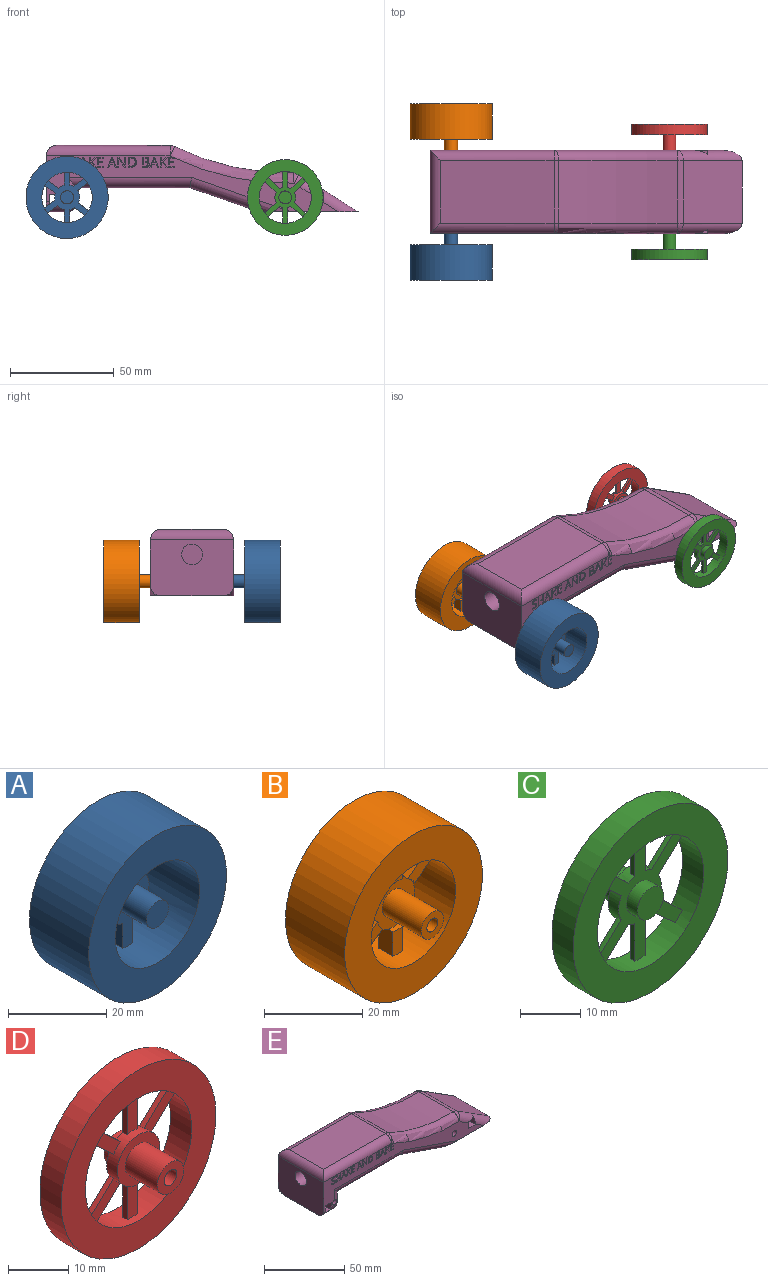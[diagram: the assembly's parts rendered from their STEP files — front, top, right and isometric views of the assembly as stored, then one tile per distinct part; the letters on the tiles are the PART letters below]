
ASSEMBLY  parts=5 mates=4
PART A: 42 faces, bbox 39.6x22.4x39.6 mm
  f0: cylinder r=12.1mm len=24.2mm, axis (0,1,0), area 1225mm2, adj f2,f3,f4,f5,f6,f7,f8,f9
  f1: cylinder r=19.8mm len=39.6mm, axis (0,1,0), area 2114.9mm2, adj f2,f3
  f2: plane 39.6x39.6mm, normal (0,-1,0), area 771.7mm2, adj f0,f1
  f3: plane 39.6x39.6mm, normal (0,1,0), area 771.7mm2, adj f0,f1
  f4: plane 6.21x2.8mm, normal (0,1,0), area 17mm2, adj f0,f15,f16,f17
  f5: plane 24.22x21.29mm, normal (0,-1,0), area 186.2mm2, adj f0,f15,f16,f18,f19,f20,f22,f23
  f6: plane 6.21x2.8mm, normal (0,1,0), area 17mm2, adj f0,f19,f20,f21
  f7: plane 7.08x5.81mm, normal (0,1,0), area 17.6mm2, adj f0,f23,f24,f25
  f8: plane 6.48x6.25mm, normal (0,1,0), area 17.6mm2, adj f0,f28,f29,f30
  f9: plane 6.48x5.97mm, normal (0,1,0), area 17mm2, adj f0,f32,f33,f34
  f10: plane 6.85x5.92mm, normal (0,1,0), area 17.5mm2, adj f0,f37,f38,f39
  f11: cylinder r=3.17mm len=11.2mm, axis (0,1,0), area 223.1mm2, adj f13,f26
  f12: cylinder r=1.57mm len=13.9mm, axis (0,1,0), area 137.1mm2, adj f13,f14
  f13: plane 6.34x6.34mm, normal (0,1,0), area 23.8mm2, adj f11,f12
  f14: plane 3.14x3.14mm, normal (0,1,0), area 7.7mm2, adj f12
  f15: plane 6.11x4mm, normal (1,0,0), area 24.4mm2, adj f0,f4,f5,f17,f27
  f16: plane 6.12x4mm, normal (-1,0,0), area 24.5mm2, adj f0,f4,f5,f17,f18
  f17: cylinder r=6.07mm len=2.8mm, axis (0,-1,0), area 3.7mm2, adj f4,f15,f16,f26
  f18: cylinder r=6.07mm len=2.75mm, axis (0,-1,0), area 8.6mm2, adj f5,f16,f26,f34
  f19: plane 6.12x4mm, normal (-1,0,0), area 24.5mm2, adj f0,f5,f6,f21,f35
  f20: plane 6.11x4mm, normal (1,0,0), area 24.4mm2, adj f0,f5,f6,f21,f22
  f21: cylinder r=6.07mm len=2.8mm, axis (0,-1,0), area 3.7mm2, adj f6,f19,f20,f26
  f22: cylinder r=6.07mm len=2.7mm, axis (0,-1,0), area 6.8mm2, adj f5,f20,f26,f38
  f23: plane 5.22x4mm, normal (-0.59,0,0.8), area 25.4mm2, adj f0,f5,f7,f24,f26,f27
  f24: cylinder r=5.88mm len=2.07mm, axis (0,-1,0), area 3.7mm2, adj f7,f23,f25,f26
  f25: plane 5x4mm, normal (0.59,0,-0.8), area 24.4mm2, adj f0,f5,f7,f24,f26,f36
  f26: plane 12.14x12.14mm, normal (0,1,0), area 82.6mm2, adj f11,f17,f18,f21,f22,f23,f24,f25
  f27: cylinder r=6.07mm len=2.7mm, axis (0,-1,0), area 4.9mm2, adj f5,f15,f23,f26
  f28: cylinder r=5.88mm len=2.55mm, axis (0,-1,0), area 3.7mm2, adj f8,f26,f29,f30
  f29: plane 5.22x4mm, normal (-0.59,0,0.8), area 25.4mm2, adj f0,f5,f8,f26,f28,f31
  f30: plane 5x4mm, normal (0.59,0,-0.8), area 24.4mm2, adj f0,f5,f8,f26,f28,f35
  f31: cylinder r=6.07mm len=3.38mm, axis (0,-1,0), area 9.3mm2, adj f5,f26,f29,f32
  f32: plane 4.96x4mm, normal (-0.59,0,-0.8), area 24.7mm2, adj f0,f5,f9,f31,f33
  f33: cylinder r=6.07mm len=2.36mm, axis (0,-1,0), area 3.7mm2, adj f9,f26,f32,f34
  f34: plane 4.88x4mm, normal (0.59,0,0.8), area 24.3mm2, adj f0,f5,f9,f18,f33
  f35: cylinder r=6.07mm len=3.19mm, axis (0,-1,0), area 10.3mm2, adj f5,f19,f26,f30
  f36: cylinder r=6.07mm len=6.03mm, axis (0,-1,0), area 17.1mm2, adj f5,f25,f26,f39
  f37: cylinder r=5.88mm len=2.14mm, axis (0,-1,0), area 3.7mm2, adj f10,f26,f38,f39
  f38: plane 5.12x4mm, normal (-0.59,0,-0.8), area 24.9mm2, adj f0,f5,f10,f22,f26,f37
  f39: plane 5.04x4mm, normal (0.59,0,0.8), area 24.5mm2, adj f0,f5,f10,f26,f36,f37
  f40: plane 6.32x6.32mm, normal (0,-1,0), area 31.4mm2, adj f41
  f41: cylinder r=3.16mm len=8.5mm, axis (0,1,0), area 168.9mm2, adj f5,f40
PART B: 42 faces, bbox 39.6x22.4x39.6 mm
  f0: cylinder r=12.1mm len=24.2mm, axis (0,-1,0), area 1225mm2, adj f2,f3,f4,f5,f6,f7,f8,f9
  f1: cylinder r=19.8mm len=39.6mm, axis (0,-1,0), area 2114.9mm2, adj f2,f3
  f2: plane 39.6x39.6mm, normal (0,1,0), area 771.7mm2, adj f0,f1
  f3: plane 39.6x39.6mm, normal (0,-1,0), area 771.7mm2, adj f0,f1
  f4: plane 6.21x2.8mm, normal (0,-1,0), area 17mm2, adj f0,f15,f16,f17
  f5: plane 24.22x21.29mm, normal (0,1,0), area 186.3mm2, adj f0,f15,f16,f18,f19,f20,f22,f23
  f6: plane 6.21x2.8mm, normal (0,-1,0), area 17mm2, adj f0,f19,f20,f21
  f7: plane 7.08x5.81mm, normal (0,-1,0), area 17.6mm2, adj f0,f23,f24,f25
  f8: plane 6.48x6.25mm, normal (0,-1,0), area 17.6mm2, adj f0,f28,f29,f30
  f9: plane 6.48x5.97mm, normal (0,-1,0), area 17mm2, adj f0,f32,f33,f34
  f10: plane 6.85x5.92mm, normal (0,-1,0), area 17.5mm2, adj f0,f37,f38,f39
  f11: cylinder r=3.17mm len=11.2mm, axis (0,-1,0), area 223.1mm2, adj f13,f26
  f12: cylinder r=1.57mm len=13.9mm, axis (0,-1,0), area 137.1mm2, adj f13,f14
  f13: plane 6.34x6.34mm, normal (0,-1,0), area 23.8mm2, adj f11,f12
  f14: plane 3.14x3.14mm, normal (0,-1,0), area 7.7mm2, adj f12
  f15: plane 6.11x4mm, normal (1,0,0), area 24.4mm2, adj f0,f4,f5,f17,f27
  f16: plane 6.12x4mm, normal (-1,0,0), area 24.5mm2, adj f0,f4,f5,f17,f18
  f17: cylinder r=6.07mm len=2.8mm, axis (0,1,0), area 3.7mm2, adj f4,f15,f16,f26
  f18: cylinder r=6.07mm len=2.75mm, axis (0,1,0), area 8.6mm2, adj f5,f16,f26,f34
  f19: plane 6.12x4mm, normal (-1,0,0), area 24.5mm2, adj f0,f5,f6,f21,f35
  f20: plane 6.11x4mm, normal (1,0,0), area 24.4mm2, adj f0,f5,f6,f21,f22
  f21: cylinder r=6.07mm len=2.8mm, axis (0,1,0), area 3.7mm2, adj f6,f19,f20,f26
  f22: cylinder r=6.07mm len=2.7mm, axis (0,1,0), area 6.8mm2, adj f5,f20,f26,f38
  f23: plane 5.22x4mm, normal (-0.59,0,0.8), area 25.4mm2, adj f0,f5,f7,f24,f26,f27
  f24: cylinder r=5.88mm len=2.07mm, axis (0,1,0), area 3.7mm2, adj f7,f23,f25,f26
  f25: plane 5x4mm, normal (0.59,0,-0.8), area 24.4mm2, adj f0,f5,f7,f24,f26,f36
  f26: plane 12.14x12.14mm, normal (0,-1,0), area 82.6mm2, adj f11,f17,f18,f21,f22,f23,f24,f25
  f27: cylinder r=6.07mm len=2.7mm, axis (0,1,0), area 4.9mm2, adj f5,f15,f23,f26
  f28: cylinder r=5.88mm len=2.55mm, axis (0,1,0), area 3.7mm2, adj f8,f26,f29,f30
  f29: plane 5.22x4mm, normal (-0.59,0,0.8), area 25.4mm2, adj f0,f5,f8,f26,f28,f31
  f30: plane 5x4mm, normal (0.59,0,-0.8), area 24.4mm2, adj f0,f5,f8,f26,f28,f35
  f31: cylinder r=6.07mm len=3.38mm, axis (0,1,0), area 9.3mm2, adj f5,f26,f29,f32
  f32: plane 4.96x4mm, normal (-0.59,0,-0.8), area 24.7mm2, adj f0,f5,f9,f31,f33
  f33: cylinder r=6.07mm len=2.36mm, axis (0,1,0), area 3.7mm2, adj f9,f26,f32,f34
  f34: plane 4.88x4mm, normal (0.59,0,0.8), area 24.3mm2, adj f0,f5,f9,f18,f33
  f35: cylinder r=6.07mm len=3.19mm, axis (0,1,0), area 10.3mm2, adj f5,f19,f26,f30
  f36: cylinder r=6.07mm len=6.03mm, axis (0,1,0), area 17.1mm2, adj f5,f25,f26,f39
  f37: cylinder r=5.88mm len=2.14mm, axis (0,1,0), area 3.7mm2, adj f10,f26,f38,f39
  f38: plane 5.12x4mm, normal (-0.59,0,-0.8), area 24.9mm2, adj f0,f5,f10,f22,f26,f37
  f39: plane 5.04x4mm, normal (0.59,0,0.8), area 24.5mm2, adj f0,f5,f10,f26,f36,f37
  f40: plane 6.32x6.32mm, normal (0,1,0), area 31.4mm2, adj f41
  f41: cylinder r=3.16mm len=8.5mm, axis (0,-1,0), area 168.9mm2, adj f5,f40
PART C: 31 faces, bbox 36.4x12.5x36.4 mm
  f0: cylinder r=3.1mm len=7.5mm, axis (0,1,0), area 146.1mm2, adj f2,f5
  f1: cylinder r=1.5mm len=10mm, axis (0,1,0), area 94.2mm2, adj f2,f3
  f2: plane 6.2x6.2mm, normal (0,1,0), area 23.1mm2, adj f0,f1
  f3: plane 3x3mm, normal (0,1,0), area 7.1mm2, adj f1
  f4: cylinder r=5mm len=10mm, axis (0,-1,0), area 64mm2, adj f5,f6,f9,f10,f11,f12,f13,f14
  f5: plane 10x10mm, normal (0,1,0), area 48.3mm2, adj f0,f4
  f6: plane 25.02x19.87mm, normal (0,-1,0), area 156.8mm2, adj f4,f8,f9,f10,f12,f13,f15,f16
  f7: plane 6.18x6.18mm, normal (0,-1,0), area 30mm2, adj f8
  f8: cylinder r=3.09mm len=6.18mm, axis (0,1,0), area 48.5mm2, adj f6,f7
  f9: plane 5.55x5.17mm, normal (0.68,0,-0.73), area 7.6mm2, adj f4,f6,f11,f27
  f10: plane 5.55x5.17mm, normal (-0.68,0,0.73), area 7.6mm2, adj f4,f6,f11,f27
  f11: plane 7.19x6.93mm, normal (0,1,0), area 18.1mm2, adj f4,f9,f10,f27
  f12: plane 7.59x1mm, normal (1,0,0), area 7.6mm2, adj f4,f6,f14,f27
  f13: plane 7.59x1mm, normal (-1,0,0), area 7.6mm2, adj f4,f6,f14,f27
  f14: plane 7.65x2.4mm, normal (0,1,0), area 18.1mm2, adj f4,f12,f13,f27
  f15: plane 5.55x5.17mm, normal (-0.68,0,-0.73), area 7.6mm2, adj f4,f6,f17,f27
  f16: plane 5.55x5.17mm, normal (0.68,0,0.73), area 7.6mm2, adj f4,f6,f17,f27
  f17: plane 7.19x6.93mm, normal (0,1,0), area 18.1mm2, adj f4,f15,f16,f27
  f18: plane 5.55x5.17mm, normal (-0.68,0,0.73), area 7.6mm2, adj f4,f6,f20,f27
  f19: plane 5.55x5.17mm, normal (0.68,0,-0.73), area 7.6mm2, adj f4,f6,f20,f27
  f20: plane 7.19x6.93mm, normal (0,1,0), area 18.1mm2, adj f4,f18,f19,f27
  f21: plane 7.59x1mm, normal (-1,0,0), area 7.6mm2, adj f4,f6,f23,f27
  f22: plane 7.59x1mm, normal (1,0,0), area 7.6mm2, adj f4,f6,f23,f27
  f23: plane 7.65x2.4mm, normal (0,1,0), area 18.1mm2, adj f4,f21,f22,f27
  f24: plane 5.55x5.17mm, normal (-0.68,0,-0.73), area 7.6mm2, adj f4,f6,f26,f27
  f25: plane 5.55x5.17mm, normal (0.68,0,0.73), area 7.6mm2, adj f4,f6,f26,f27
  f26: plane 7.19x6.93mm, normal (0,1,0), area 18.1mm2, adj f4,f24,f25,f27
  f27: cylinder r=12.5mm len=25mm, axis (0,1,0), area 378.3mm2, adj f6,f9,f10,f11,f12,f13,f14,f15
  f28: cylinder r=18.2mm len=36.4mm, axis (0,1,0), area 571.8mm2, adj f29,f30
  f29: plane 36.4x36.4mm, normal (0,-1,0), area 549.7mm2, adj f27,f28
  f30: plane 36.4x36.4mm, normal (0,1,0), area 549.7mm2, adj f27,f28
PART D: 31 faces, bbox 36.4x12.5x36.4 mm
  f0: cylinder r=3.1mm len=7.5mm, axis (0,-1,0), area 146.1mm2, adj f2,f5
  f1: cylinder r=1.5mm len=10mm, axis (0,-1,0), area 94.2mm2, adj f2,f3
  f2: plane 6.2x6.2mm, normal (0,-1,0), area 23.1mm2, adj f0,f1
  f3: plane 3x3mm, normal (0,-1,0), area 7.1mm2, adj f1
  f4: cylinder r=5mm len=10mm, axis (0,1,0), area 64mm2, adj f5,f6,f9,f10,f11,f12,f13,f14
  f5: plane 10x10mm, normal (0,-1,0), area 48.3mm2, adj f0,f4
  f6: plane 25.02x19.87mm, normal (0,1,0), area 156.8mm2, adj f4,f8,f9,f10,f12,f13,f15,f16
  f7: plane 6.18x6.18mm, normal (0,1,0), area 30mm2, adj f8
  f8: cylinder r=3.09mm len=6.18mm, axis (0,-1,0), area 48.5mm2, adj f6,f7
  f9: plane 5.55x5.17mm, normal (0.68,0,-0.73), area 7.6mm2, adj f4,f6,f11,f27
  f10: plane 5.55x5.17mm, normal (-0.68,0,0.73), area 7.6mm2, adj f4,f6,f11,f27
  f11: plane 7.19x6.93mm, normal (0,-1,0), area 18.1mm2, adj f4,f9,f10,f27
  f12: plane 7.59x1mm, normal (1,0,0), area 7.6mm2, adj f4,f6,f14,f27
  f13: plane 7.59x1mm, normal (-1,0,0), area 7.6mm2, adj f4,f6,f14,f27
  f14: plane 7.65x2.4mm, normal (0,-1,0), area 18.1mm2, adj f4,f12,f13,f27
  f15: plane 5.55x5.17mm, normal (-0.68,0,-0.73), area 7.6mm2, adj f4,f6,f17,f27
  f16: plane 5.55x5.17mm, normal (0.68,0,0.73), area 7.6mm2, adj f4,f6,f17,f27
  f17: plane 7.19x6.93mm, normal (0,-1,0), area 18.1mm2, adj f4,f15,f16,f27
  f18: plane 5.55x5.17mm, normal (-0.68,0,0.73), area 7.6mm2, adj f4,f6,f20,f27
  f19: plane 5.55x5.17mm, normal (0.68,0,-0.73), area 7.6mm2, adj f4,f6,f20,f27
  f20: plane 7.19x6.93mm, normal (0,-1,0), area 18.1mm2, adj f4,f18,f19,f27
  f21: plane 7.59x1mm, normal (-1,0,0), area 7.6mm2, adj f4,f6,f23,f27
  f22: plane 7.59x1mm, normal (1,0,0), area 7.6mm2, adj f4,f6,f23,f27
  f23: plane 7.65x2.4mm, normal (0,-1,0), area 18.1mm2, adj f4,f21,f22,f27
  f24: plane 5.55x5.17mm, normal (-0.68,0,-0.73), area 7.6mm2, adj f4,f6,f26,f27
  f25: plane 5.55x5.17mm, normal (0.68,0,0.73), area 7.6mm2, adj f4,f6,f26,f27
  f26: plane 7.19x6.93mm, normal (0,-1,0), area 18.1mm2, adj f4,f24,f25,f27
  f27: cylinder r=12.5mm len=25mm, axis (0,-1,0), area 378.3mm2, adj f6,f9,f10,f11,f12,f13,f14,f15
  f28: cylinder r=18.2mm len=36.4mm, axis (0,-1,0), area 571.8mm2, adj f29,f30
  f29: plane 36.4x36.4mm, normal (0,1,0), area 549.7mm2, adj f27,f28
  f30: plane 36.4x36.4mm, normal (0,-1,0), area 549.7mm2, adj f27,f28
PART E: 246 faces, bbox 150x40x36.7 mm
  f0: cylinder r=5mm len=0.13mm, axis (0,0,1), area 0mm2, adj f2,f9,f244
  f1: cylinder r=5mm len=11.7mm, axis (0,0,-1), area 59.9mm2, adj f3,f9,f30,f237,f239
  f2: plane 140.79x27mm, normal (0,-1,0), area 1223.2mm2, adj f0,f4,f5,f9,f10,f15,f21,f26
  f3: plane 140.79x27mm, normal (0,1,0), area 1319.6mm2, adj f1,f4,f5,f9,f10,f16,f19,f24
  f4: plane 46.54x40mm, normal (0,0,-1), area 1815mm2, adj f2,f3,f14,f15,f16,f28,f236,f241
  f5: plane 40x27mm, normal (-1,0,0), area 990.7mm2, adj f2,f3,f6,f7,f23,f240,f245
  f6: plane 30x9.87mm, normal (0,0,-1), area 296.1mm2, adj f5,f235,f240,f245
  f7: cylinder r=5mm len=60mm, axis (-1,0,0), area 1885mm2, adj f5,f8
  f8: plane 10x10mm, normal (-1,0,0), area 78.5mm2, adj f7
  f9: cylinder r=2mm len=40mm, axis (0,-1,0), area 499.6mm2, adj f0,f1,f2,f3,f238,f243
  f10: cylinder r=2mm len=40mm, axis (0,-1,0), area 502.7mm2, adj f2,f3
  f11: plane 54.55x30mm, normal (0,0,1), area 1636.4mm2, adj f20,f21,f23,f24
  f12: cylinder r=121.86mm len=57.18mm, axis (0,-1,0), area 1773.9mm2, adj f17,f19,f20,f26
  f13: plane 30x28.24mm, normal (0.54,0,0.84), area 1005.1mm2, adj f14,f15,f16,f17
  f14: cylinder r=5mm len=34.16mm, axis (0,1,0), area 24.9mm2, adj f4,f13,f15,f16
  f15: cylinder r=5mm len=30.93mm, axis (-0.84,0,0.54), area 223mm2, adj f2,f4,f13,f14,f25,f32,f33,f34
  f16: cylinder r=5mm len=30.93mm, axis (0.84,0,-0.54), area 223mm2, adj f3,f4,f13,f14,f18,f32,f33,f34
  f17: cylinder r=5mm len=30mm, axis (0,-1,0), area 89mm2, adj f12,f13,f18,f25
  f18: sphere r=5mm, area 14.8mm2, adj f16,f17,f19
  f19: torus R=126.86mm, axis (0,-1,0), area 471.3mm2, adj f3,f12,f18,f22
  f20: cylinder r=5mm len=30mm, axis (0,-1,0), area 69mm2, adj f11,f12,f22,f27
  f21: cylinder r=5mm len=59.55mm, axis (-1,0,0), area 453.4mm2, adj f2,f11,f23,f27
  f22: sphere r=5mm, area 11.5mm2, adj f19,f20,f24
  f23: cylinder r=5mm len=40mm, axis (0,-1,0), area 285.6mm2, adj f5,f11,f21,f24
  f24: cylinder r=5mm len=59.55mm, axis (1,0,0), area 453.4mm2, adj f3,f11,f22,f23
  f25: sphere r=5mm, area 14.8mm2, adj f15,f17,f26
  f26: torus R=126.86mm, axis (0,-1,0), area 471.2mm2, adj f2,f12,f25,f27,f47,f48
  f27: sphere r=5mm, area 11.5mm2, adj f20,f21,f26
  f28: plane 33.64x30mm, normal (-0.33,0,-0.94), area 1068.5mm2, adj f4,f29,f236,f241
  f29: plane 54.2x30mm, normal (0,0,-1), area 1625.9mm2, adj f28,f30,f237,f242
  f30: plane 30x6.7mm, normal (1,0,0), area 201mm2, adj f1,f29,f235,f243
  f31: plane 40x6.08mm, normal (0,0,1), area 243.2mm2, adj f2,f3,f32,f33
  f32: plane 40x5.07mm, normal (1,0,0), area 202.6mm2, adj f2,f3,f15,f16,f31,f34
  f33: plane 40x5.07mm, normal (-1,0,0), area 196.8mm2, adj f2,f3,f15,f16,f31,f34
  f34: plane 39.89x6.08mm, normal (0,0,-1), area 234.1mm2, adj f15,f16,f32,f33
  f35: plane 40x5.58mm, normal (1,0,0), area 222.6mm2, adj f2,f3,f36,f38,f240,f245
  f36: plane 39.17x5.11mm, normal (0,0,1), area 200mm2, adj f35,f37,f240,f245
  f37: plane 40x5.58mm, normal (-1,0,0), area 222.6mm2, adj f2,f3,f36,f38,f240,f245
  f38: plane 40x5.11mm, normal (0,0,-1), area 204.3mm2, adj f2,f3,f35,f37
  f39: plane 1x0.5mm, normal (-1,0,0), area 0.5mm2, adj f2,f40,f50,f51
  f40: plane 2.12x1mm, normal (0,0,-1), area 2.1mm2, adj f2,f39,f41,f51
  f41: plane 1.77x1mm, normal (-1,0,0), area 1.8mm2, adj f2,f40,f42,f51
  f42: plane 1.99x1mm, normal (0,0,1), area 2mm2, adj f2,f41,f43,f51
  f43: plane 1x0.49mm, normal (-1,0,0), area 0.5mm2, adj f2,f42,f44,f51
  f44: plane 1.99x1mm, normal (0,0,-1), area 2mm2, adj f2,f43,f45,f51
  f45: plane 1.55x1mm, normal (-1,0,0), area 1.5mm2, adj f2,f44,f46,f51
  f46: plane 2.12x1mm, normal (0,0,1), area 2.1mm2, adj f2,f45,f47,f51
  f47: plane 1x0.5mm, normal (-1,0,0), area 0.5mm2, adj f2,f26,f46,f48,f51
  f48: plane 2.68x1mm, normal (0,0,-1), area 2.7mm2, adj f2,f26,f47,f49,f51
  f49: plane 4.8x1mm, normal (1,0,0), area 4.8mm2, adj f2,f48,f50,f51
  f50: plane 2.68x1mm, normal (0,0,1), area 2.7mm2, adj f2,f39,f49,f51
  f51: plane 4.8x2.68mm, normal (0,-1,0), area 5.8mm2, adj f39,f40,f41,f42,f43,f44,f45,f46
  f52: plane 1x0.58mm, normal (0,0,1), area 0.6mm2, adj f2,f53,f64,f65
  f53: plane 4.82x1.89mm, normal (-0.93,0,-0.36), area 5.2mm2, adj f2,f52,f54,f65
  f54: plane 1x0.47mm, normal (0,0,-1), area 0.5mm2, adj f2,f53,f55,f65
  f55: plane 4.82x1.9mm, normal (0.93,0,-0.37), area 5.2mm2, adj f2,f54,f56,f65
  f56: plane 1x0.57mm, normal (0,0,1), area 0.6mm2, adj f2,f55,f57,f65
  f57: plane 1.53x1mm, normal (-0.93,0,0.36), area 1.6mm2, adj f2,f56,f58,f65
  f58: plane 1.92x1mm, normal (0,0,1), area 1.9mm2, adj f2,f57,f64,f65
  f59: plane 1.55x1mm, normal (0,0,-1), area 1.6mm2, adj f60,f63,f65,f66
  f60: plane 1.49x1mm, normal (-0.94,0,0.35), area 1.6mm2, adj f59,f61,f65,f66
  f61: extruded ~1x0.69mm, area 0.7mm2, adj f60,f62,f65,f66
  f62: extruded ~1x0.69mm, area 0.7mm2, adj f61,f63,f65,f66
  f63: plane 1.49x1mm, normal (0.94,0,0.35), area 1.6mm2, adj f59,f62,f65,f66
  f64: plane 1.53x1mm, normal (0.93,0,0.36), area 1.6mm2, adj f2,f52,f58,f65
  f65: plane 4.82x4.25mm, normal (0,-1,0), area 5.9mm2, adj f52,f53,f54,f55,f56,f57,f58,f59
  f66: plane 2.18x1.55mm, normal (0,-1,0), area 1.6mm2, adj f59,f60,f61,f62,f63
  f67: plane 1x0.58mm, normal (0,0,1), area 0.6mm2, adj f2,f68,f79,f80
  f68: plane 4.82x1.89mm, normal (-0.93,0,-0.36), area 5.2mm2, adj f2,f67,f69,f80
  f69: plane 1x0.47mm, normal (0,0,-1), area 0.5mm2, adj f2,f68,f70,f80
  f70: plane 4.82x1.9mm, normal (0.93,0,-0.37), area 5.2mm2, adj f2,f69,f71,f80
  f71: plane 1x0.57mm, normal (0,0,1), area 0.6mm2, adj f2,f70,f72,f80
  f72: plane 1.53x1mm, normal (-0.93,0,0.36), area 1.6mm2, adj f2,f71,f73,f80
  f73: plane 1.92x1mm, normal (0,0,1), area 1.9mm2, adj f2,f72,f79,f80
  f74: plane 1.55x1mm, normal (0,0,-1), area 1.6mm2, adj f75,f78,f80,f81
  f75: plane 1.49x1mm, normal (-0.94,0,0.35), area 1.6mm2, adj f74,f76,f80,f81
  f76: extruded ~1x0.69mm, area 0.7mm2, adj f75,f77,f80,f81
  f77: extruded ~1x0.69mm, area 0.7mm2, adj f76,f78,f80,f81
  f78: plane 1.49x1mm, normal (0.94,0,0.35), area 1.6mm2, adj f74,f77,f80,f81
  f79: plane 1.53x1mm, normal (0.93,0,0.36), area 1.6mm2, adj f2,f67,f73,f80
  f80: plane 4.82x4.25mm, normal (0,-1,0), area 5.9mm2, adj f67,f68,f69,f70,f71,f72,f73,f74
  f81: plane 2.18x1.55mm, normal (0,-1,0), area 1.6mm2, adj f74,f75,f76,f77,f78
  f82: plane 2.71x2mm, normal (-0.8,0,-0.59), area 3.4mm2, adj f2,f83,f93,f94
  f83: plane 2.09x1.93mm, normal (-0.73,0,0.68), area 2.8mm2, adj f2,f82,f84,f94
  f84: plane 1x0.66mm, normal (0,0,-1), area 0.7mm2, adj f2,f83,f85,f94
  f85: plane 2.38x2.18mm, normal (0.74,0,-0.67), area 3.2mm2, adj f2,f84,f86,f94
  f86: plane 2.38x1mm, normal (-1,0,0), area 2.4mm2, adj f2,f85,f87,f94
  f87: plane 1x0.56mm, normal (0,0,-1), area 0.6mm2, adj f2,f86,f88,f94
  f88: plane 4.8x1mm, normal (1,0,0), area 4.8mm2, adj f2,f87,f89,f94
  f89: plane 1x0.56mm, normal (0,0,1), area 0.6mm2, adj f2,f88,f90,f94
  f90: plane 1.88x1mm, normal (-1,0,0), area 1.9mm2, adj f2,f89,f91,f94
  f91: plane 1x0.5mm, normal (-0.66,0,0.75), area 0.7mm2, adj f2,f90,f92,f94
  f92: plane 2.33x1.75mm, normal (0.8,0,0.6), area 2.9mm2, adj f2,f91,f93,f94
  f93: plane 1x0.66mm, normal (0,0,1), area 0.7mm2, adj f2,f82,f92,f94
  f94: plane 4.8x3.47mm, normal (0,-1,0), area 6.1mm2, adj f82,f83,f84,f85,f86,f87,f88,f89
  f95: plane 4.8x1mm, normal (-1,0,0), area 4.8mm2, adj f2,f96,f109,f110
  f96: plane 1x0.52mm, normal (0,0,-1), area 0.5mm2, adj f2,f95,f97,f110
  f97: plane 2.75x1mm, normal (1,0,0), area 2.8mm2, adj f2,f96,f98,f110
  f98: extruded ~1x0.69mm, area 0.7mm2, adj f2,f97,f99,f110
  f99: extruded ~1x0.57mm, area 0.6mm2, adj f2,f98,f100,f110
  f100: plane 1x0.03mm, normal (0,0,-1), area 0mm2, adj f2,f99,f101,f110
  f101: plane 4.01x2.62mm, normal (-0.84,0,-0.55), area 4.8mm2, adj f2,f100,f102,f110
  f102: plane 1x0.63mm, normal (0,0,-1), area 0.6mm2, adj f2,f101,f103,f110
  f103: plane 4.8x1mm, normal (1,0,0), area 4.8mm2, adj f2,f102,f104,f110
  f104: plane 1x0.52mm, normal (0,0,1), area 0.5mm2, adj f2,f103,f105,f110
  f105: plane 2.73x1mm, normal (-1,0,0), area 2.7mm2, adj f2,f104,f106,f110
  f106: extruded ~1.3x1mm, area 1.3mm2, adj f2,f105,f107,f110
  f107: plane 1x0.03mm, normal (0,0,1), area 0mm2, adj f2,f106,f108,f110
  f108: plane 4.03x2.62mm, normal (0.84,0,0.55), area 4.8mm2, adj f2,f107,f109,f110
  f109: plane 1x0.64mm, normal (0,0,1), area 0.6mm2, adj f2,f95,f108,f110
  f110: plane 4.8x3.75mm, normal (0,-1,0), area 7.6mm2, adj f95,f96,f97,f98,f99,f100,f101,f102
  f111: plane 1x0.5mm, normal (-1,0,0), area 0.5mm2, adj f2,f112,f122,f123
  f112: plane 2.12x1mm, normal (0,0,-1), area 2.1mm2, adj f2,f111,f113,f123
  f113: plane 1.77x1mm, normal (-1,0,0), area 1.8mm2, adj f2,f112,f114,f123
  f114: plane 1.99x1mm, normal (0,0,1), area 2mm2, adj f2,f113,f115,f123
  f115: plane 1x0.49mm, normal (-1,0,0), area 0.5mm2, adj f2,f114,f116,f123
  f116: plane 1.99x1mm, normal (0,0,-1), area 2mm2, adj f2,f115,f117,f123
  f117: plane 1.55x1mm, normal (-1,0,0), area 1.5mm2, adj f2,f116,f118,f123
  f118: plane 2.12x1mm, normal (0,0,1), area 2.1mm2, adj f2,f117,f119,f123
  f119: plane 1x0.5mm, normal (-1,0,0), area 0.5mm2, adj f2,f118,f120,f123
  f120: plane 2.68x1mm, normal (0,0,-1), area 2.7mm2, adj f2,f119,f121,f123
  f121: plane 4.8x1mm, normal (1,0,0), area 4.8mm2, adj f2,f120,f122,f123
  f122: plane 2.68x1mm, normal (0,0,1), area 2.7mm2, adj f2,f111,f121,f123
  f123: plane 4.8x2.68mm, normal (0,-1,0), area 5.8mm2, adj f111,f112,f113,f114,f115,f116,f117,f118
  f124: plane 2.71x2mm, normal (-0.8,0,-0.59), area 3.4mm2, adj f2,f125,f135,f136
  f125: plane 2.09x1.93mm, normal (-0.73,0,0.68), area 2.8mm2, adj f2,f124,f126,f136
  f126: plane 1x0.66mm, normal (0,0,-1), area 0.7mm2, adj f2,f125,f127,f136
  f127: plane 2.38x2.18mm, normal (0.74,0,-0.67), area 3.2mm2, adj f2,f126,f128,f136
  f128: plane 2.38x1mm, normal (-1,0,0), area 2.4mm2, adj f2,f127,f129,f136
  f129: plane 1x0.56mm, normal (0,0,-1), area 0.6mm2, adj f2,f128,f130,f136
  f130: plane 4.8x1mm, normal (1,0,0), area 4.8mm2, adj f2,f129,f131,f136
  f131: plane 1x0.56mm, normal (0,0,1), area 0.6mm2, adj f2,f130,f132,f136
  f132: plane 1.88x1mm, normal (-1,0,0), area 1.9mm2, adj f2,f131,f133,f136
  f133: plane 1x0.5mm, normal (-0.66,0,0.75), area 0.7mm2, adj f2,f132,f134,f136
  f134: plane 2.33x1.75mm, normal (0.8,0,0.6), area 2.9mm2, adj f2,f133,f135,f136
  f135: plane 1x0.66mm, normal (0,0,1), area 0.7mm2, adj f2,f124,f134,f136
  f136: plane 4.8x3.47mm, normal (0,-1,0), area 6.1mm2, adj f124,f125,f126,f127,f128,f129,f130,f131
  f137: plane 4.8x1mm, normal (-1,0,0), area 4.8mm2, adj f2,f138,f148,f149
  f138: plane 1x0.56mm, normal (0,0,-1), area 0.6mm2, adj f2,f137,f139,f149
  f139: plane 2.04x1mm, normal (1,0,0), area 2mm2, adj f2,f138,f140,f149
  f140: plane 2.53x1mm, normal (0,0,-1), area 2.5mm2, adj f2,f139,f141,f149
  f141: plane 2.04x1mm, normal (-1,0,0), area 2mm2, adj f2,f140,f142,f149
  f142: plane 1x0.56mm, normal (0,0,-1), area 0.6mm2, adj f2,f141,f143,f149
  f143: plane 4.8x1mm, normal (1,0,0), area 4.8mm2, adj f2,f142,f144,f149
  f144: plane 1x0.56mm, normal (0,0,1), area 0.6mm2, adj f2,f143,f145,f149
  f145: plane 2.26x1mm, normal (-1,0,0), area 2.3mm2, adj f2,f144,f146,f149
  f146: plane 2.53x1mm, normal (0,0,1), area 2.5mm2, adj f2,f145,f147,f149
  f147: plane 2.26x1mm, normal (1,0,0), area 2.3mm2, adj f2,f146,f148,f149
  f148: plane 1x0.56mm, normal (0,0,1), area 0.6mm2, adj f2,f137,f147,f149
  f149: plane 4.8x3.64mm, normal (0,-1,0), area 6.6mm2, adj f137,f138,f139,f140,f141,f142,f143,f144
  f150: plane 4.8x1mm, normal (1,0,0), area 4.8mm2, adj f2,f151,f174,f175
  f151: plane 1.67x1mm, normal (0,0,1), area 1.7mm2, adj f2,f150,f152,f175
  f152: extruded ~1.22x1mm, area 1.3mm2, adj f2,f151,f153,f175
  f153: extruded ~1x1mm, area 1.1mm2, adj f2,f152,f154,f175
  f154: extruded ~1.15x1.09mm, area 1.8mm2, adj f2,f153,f155,f175
  f155: plane 1x0.03mm, normal (-1,0,0), area 0mm2, adj f2,f154,f156,f175
  f156: extruded ~1x0.7mm, area 0.8mm2, adj f2,f155,f157,f175
  f157: extruded ~1x0.71mm, area 0.8mm2, adj f2,f156,f158,f175
  f158: extruded ~1x0.9mm, area 1mm2, adj f2,f157,f159,f175
  f159: extruded ~1.38x1mm, area 1.4mm2, adj f2,f158,f174,f175
  f160: plane 1.57x1mm, normal (-1,0,0), area 1.6mm2, adj f161,f172,f175,f177
  f161: plane 1x0.82mm, normal (0,0,1), area 0.8mm2, adj f160,f162,f175,f177
  f162: extruded ~1x0.92mm, area 0.9mm2, adj f161,f163,f175,f177
  f163: extruded ~1x0.58mm, area 0.7mm2, adj f162,f164,f175,f177
  f164: extruded ~1x0.62mm, area 0.7mm2, adj f163,f165,f175,f177
  f165: extruded ~1x0.85mm, area 0.9mm2, adj f164,f172,f175,f177
  f166: plane 1x0.96mm, normal (0,0,1), area 1mm2, adj f167,f173,f175,f176
  f167: extruded ~1x0.91mm, area 1mm2, adj f166,f168,f175,f176
  f168: extruded ~1x0.66mm, area 0.8mm2, adj f167,f169,f175,f176
  f169: extruded ~1x0.71mm, area 0.8mm2, adj f168,f170,f175,f176
  f170: extruded ~1x0.87mm, area 0.9mm2, adj f169,f171,f175,f176
  f171: plane 1x1mm, normal (0,0,-1), area 1mm2, adj f170,f173,f175,f176
  f172: plane 1x0.92mm, normal (0,0,-1), area 0.9mm2, adj f160,f165,f175,f177
  f173: plane 1.8x1mm, normal (-1,0,0), area 1.8mm2, adj f166,f171,f175,f176
  f174: plane 1.36x1mm, normal (0,0,-1), area 1.4mm2, adj f2,f150,f159,f175
  f175: plane 4.8x3.33mm, normal (0,-1,0), area 7.9mm2, adj f150,f151,f152,f153,f154,f155,f156,f157
  f176: plane 2.17x1.8mm, normal (0,-1,0), area 3.6mm2, adj f166,f167,f168,f169,f170,f171,f173
  f177: plane 2.03x1.57mm, normal (0,-1,0), area 2.9mm2, adj f160,f161,f162,f163,f164,f165,f172
  f178: plane 1x0.58mm, normal (0,0,1), area 0.6mm2, adj f2,f179,f190,f191
  f179: plane 4.82x1.89mm, normal (-0.93,0,-0.36), area 5.2mm2, adj f2,f178,f180,f191
  f180: plane 1x0.47mm, normal (0,0,-1), area 0.5mm2, adj f2,f179,f181,f191
  f181: plane 4.82x1.9mm, normal (0.93,0,-0.37), area 5.2mm2, adj f2,f180,f182,f191
  f182: plane 1x0.57mm, normal (0,0,1), area 0.6mm2, adj f2,f181,f183,f191
  f183: plane 1.53x1mm, normal (-0.93,0,0.36), area 1.6mm2, adj f2,f182,f184,f191
  f184: plane 1.92x1mm, normal (0,0,1), area 1.9mm2, adj f2,f183,f190,f191
  f185: plane 1.55x1mm, normal (0,0,-1), area 1.6mm2, adj f186,f189,f191,f192
  f186: plane 1.49x1mm, normal (-0.94,0,0.35), area 1.6mm2, adj f185,f187,f191,f192
  f187: extruded ~1x0.69mm, area 0.7mm2, adj f186,f188,f191,f192
  f188: extruded ~1x0.69mm, area 0.7mm2, adj f187,f189,f191,f192
  f189: plane 1.49x1mm, normal (0.94,0,0.35), area 1.6mm2, adj f185,f188,f191,f192
  f190: plane 1.53x1mm, normal (0.93,0,0.36), area 1.6mm2, adj f2,f178,f184,f191
  f191: plane 4.82x4.25mm, normal (0,-1,0), area 5.9mm2, adj f178,f179,f180,f181,f182,f183,f184,f185
  f192: plane 2.18x1.55mm, normal (0,-1,0), area 1.6mm2, adj f185,f186,f187,f188,f189
  f193: extruded ~1.73x1mm, area 1.9mm2, adj f2,f194,f206,f207
  f194: extruded ~1.74x1mm, area 1.9mm2, adj f2,f193,f195,f207
  f195: plane 1.47x1mm, normal (0,0,-1), area 1.5mm2, adj f2,f194,f196,f207
  f196: plane 4.8x1mm, normal (1,0,0), area 4.8mm2, adj f2,f195,f197,f207
  f197: plane 1.33x1mm, normal (0,0,1), area 1.3mm2, adj f2,f196,f198,f207
  f198: extruded ~1.86x1mm, area 2mm2, adj f2,f197,f206,f207
  f199: extruded ~1.45x1mm, area 1.6mm2, adj f200,f205,f207,f208
  f200: extruded ~1.5x1mm, area 1.6mm2, adj f199,f201,f207,f208
  f201: plane 1x0.68mm, normal (0,0,-1), area 0.7mm2, adj f200,f202,f207,f208
  f202: plane 3.83x1mm, normal (-1,0,0), area 3.8mm2, adj f201,f203,f207,f208
  f203: plane 1x0.81mm, normal (0,0,1), area 0.8mm2, adj f202,f204,f207,f208
  f204: extruded ~1.4x1mm, area 1.5mm2, adj f203,f205,f207,f208
  f205: extruded ~1.42x1mm, area 1.5mm2, adj f199,f204,f207,f208
  f206: extruded ~1.82x1mm, area 2mm2, adj f2,f193,f198,f207
  f207: plane 4.8x3.83mm, normal (0,-1,0), area 7.3mm2, adj f193,f194,f195,f196,f197,f198,f199,f200
  f208: plane 3.83x2.68mm, normal (0,-1,0), area 9mm2, adj f199,f200,f201,f202,f203,f204,f205
  f209: extruded ~1x0.8mm, area 0.9mm2, adj f2,f210,f233,f234
  f210: extruded ~1.04x1mm, area 1.2mm2, adj f2,f209,f211,f234
  f211: extruded ~1x0.67mm, area 0.7mm2, adj f2,f210,f212,f234
  f212: extruded ~1x0.31mm, area 0.4mm2, adj f2,f211,f213,f234
  f213: extruded ~1x0.41mm, area 0.4mm2, adj f2,f212,f214,f234
  f214: extruded ~1x0.53mm, area 0.6mm2, adj f2,f213,f215,f234
  f215: extruded ~1x0.69mm, area 0.7mm2, adj f2,f214,f216,f234
  f216: extruded ~1.16x1mm, area 1.2mm2, adj f2,f215,f217,f234
  f217: plane 1x0.49mm, normal (-0.94,0,0.34), area 0.5mm2, adj f2,f216,f218,f234
  f218: extruded ~1.32x1mm, area 1.4mm2, adj f2,f217,f219,f234
  f219: extruded ~1.1x1mm, area 1.2mm2, adj f2,f218,f220,f234
  f220: extruded ~1x0.88mm, area 1mm2, adj f2,f219,f221,f234
  f221: extruded ~1x0.86mm, area 0.9mm2, adj f2,f220,f222,f234
  f222: extruded ~1x0.96mm, area 1.1mm2, adj f2,f221,f223,f234
  f223: extruded ~1x0.71mm, area 0.8mm2, adj f2,f222,f224,f234
  f224: extruded ~1x0.34mm, area 0.5mm2, adj f2,f223,f225,f234
  f225: extruded ~1x0.41mm, area 0.4mm2, adj f2,f224,f226,f234
  f226: extruded ~1x0.59mm, area 0.7mm2, adj f2,f225,f227,f234
  f227: extruded ~1x0.84mm, area 0.9mm2, adj f2,f226,f228,f234
  f228: extruded ~1x0.69mm, area 0.7mm2, adj f2,f227,f229,f234
  f229: extruded ~1x0.64mm, area 0.7mm2, adj f2,f228,f230,f234
  f230: plane 1x0.54mm, normal (1,0,0), area 0.5mm2, adj f2,f229,f231,f234
  f231: extruded ~1.31x1mm, area 1.3mm2, adj f2,f230,f232,f234
  f232: extruded ~1.25x1mm, area 1.3mm2, adj f2,f231,f233,f234
  f233: extruded ~1x0.99mm, area 1.1mm2, adj f2,f209,f232,f234
  f234: plane 4.93x3.02mm, normal (0,-1,0), area 5.3mm2, adj f209,f210,f211,f212,f213,f214,f215,f216
  f235: cylinder r=5mm len=30mm, axis (0,1,0), area 235.6mm2, adj f6,f30,f239,f244
  f236: cylinder r=5mm len=49.66mm, axis (-0.94,0,0.33), area 323.2mm2, adj f3,f4,f28,f237
  f237: cylinder r=5mm len=60.04mm, axis (-1,0,0), area 442.3mm2, adj f1,f3,f29,f236
  f238: cylinder r=5mm len=0.13mm, axis (0,0,-1), area 0mm2, adj f3,f9,f239
  f239: sphere r=5mm, area 39.3mm2, adj f1,f235,f238,f240
  f240: cylinder r=5mm len=9.87mm, axis (1,0,0), area 67.1mm2, adj f3,f5,f6,f35,f36,f37,f239
  f241: cylinder r=5mm len=49.66mm, axis (0.94,0,-0.33), area 323.2mm2, adj f2,f4,f28,f242
  f242: cylinder r=5mm len=60.04mm, axis (1,0,0), area 442.3mm2, adj f2,f29,f241,f243
  f243: cylinder r=5mm len=11.7mm, axis (0,0,1), area 59.9mm2, adj f2,f9,f30,f242,f244
  f244: sphere r=5mm, area 39.3mm2, adj f0,f235,f243,f245
  f245: cylinder r=5mm len=9.87mm, axis (-1,0,0), area 67.1mm2, adj f2,f5,f6,f35,f36,f37,f244
PLACE A t=(-90.7,-51.96,-9.23)mm
PLACE B t=(-90.7,-51.16,-9.23)mm
PLACE C t=(-0.19,-47.26,-15.09)mm
PLACE D t=(-0.19,-32.26,-15.09)mm
PLACE E t=(-30.99,-7.26,10.21)mm
MATE revolute D.f0 <-> E.f10  axis (0,-1,0) through (-0.19,-7.26,-15.09)mm
MATE revolute C.f0 <-> E.f10  axis (0,1,0) through (-0.19,-47.26,-15.09)mm
MATE revolute A.f0 <-> E.f9  axis (0,1,0) through (-105.19,-47.26,-15.09)mm
MATE revolute B.f0 <-> E.f9  axis (0,-1,0) through (-105.19,-7.26,-15.09)mm
